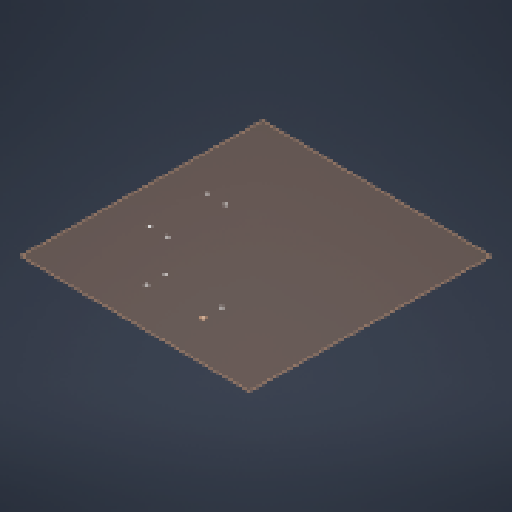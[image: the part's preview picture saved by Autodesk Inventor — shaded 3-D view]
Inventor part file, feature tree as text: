
AUTODESK INVENTOR PART (.ipt)
format: ipt  version: 2024 (Build 280153000, 153)  size: 253,952 bytes
history: native  units: mm
features: other x4, plane x2, extrude x2, sketch x2
ambient origin geometry x8: Origin, YZ Plane, XZ Plane, XY Plane, X Axis, Y Axis, Z Axis, Center Point
bodies: Body1 (feature_tree)
feature tree (10):
  other  "Sólido1"
  plane  "Plano de trabajo1"
  extrude  "Extrusión1"  Depth=600.0mm
  plane  "Plano de trabajo2"
  extrude  "Extrusión3"  Depth=6.0mm TaperAngle=0.0deg
  sketch  "Boceto1"  dims[d0=1700.0mm d1=600.0mm]
  sketch  "Boceto3"  dims[d17=80.0mm d18=80.0mm d21=10.0mm d22=15.0mm d23=15.0mm d26=6.0mm d27=0.0mm d28=0.0mm d35=30.0mm d36=30.0mm d37=25.0mm d38=25.0mm d39=30.0mm d40=30.0mm d41=25.0mm d42=25.0mm d45=15.0mm d46=15.0mm d47=15.0mm d48=15.0mm d49=15.0mm d50=15.0mm d51=15.0mm d52=30.0mm d53=30.0mm d54=25.0mm d55=25.0mm d56=30.0mm d57=30.0mm d59=25.0mm d60=25.0mm d61=2.5mm d62=0.0mm]
  other  "<userpath>\Downloads\Celda_Robotizada.iam"
  other  "Celda_Robotizada.iam"
  other  "Piso:1"
